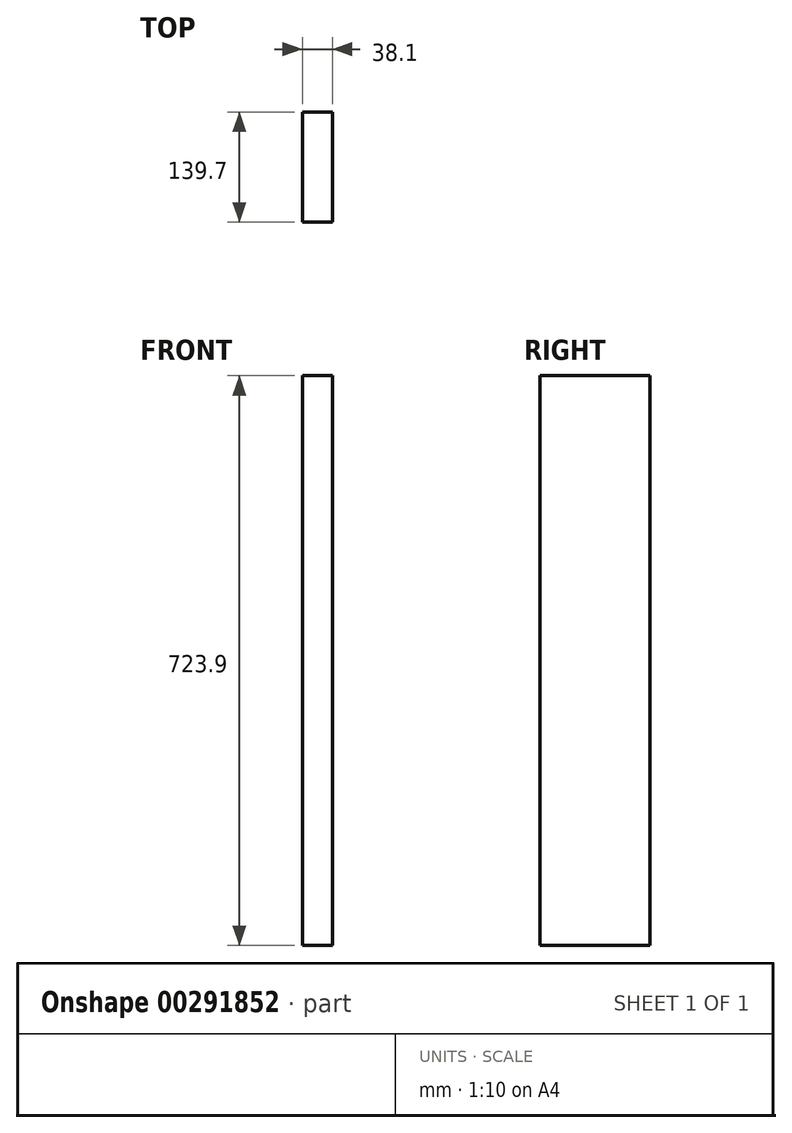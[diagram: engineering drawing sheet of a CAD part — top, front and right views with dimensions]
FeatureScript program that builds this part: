
annotation { "Feature Type Name" : "Feature", "Feature Type Description" : "" }
export const myFeature = defineFeature(function(context is Context, id is Id, definition is map)
    precondition{}
    {
        {
            var Q0;
            Q0=qCreatedBy(makeId("Top.planeOp"),FACE);
            var sketch = newSketch(context, id + "F0", { "sketchPlane" : qUnion([Q0])});
            skLineSegment(sketch, "E0.bottom", {"start": v(19.05, 69.85) * mm, "end": v(-19.05, 69.85) * mm});
            skLineSegment(sketch, "E0.top", {"start": v(19.05, -69.85) * mm, "end": v(-19.05, -69.85) * mm});
            skLineSegment(sketch, "E0.left", {"start": v(19.05, 69.85) * mm, "end": v(19.05, -69.85) * mm});
            skLineSegment(sketch, "E0.right", {"start": v(-19.05, 69.85) * mm, "end": v(-19.05, -69.85) * mm});
            skPoint(sketch, "E0.middle", {"position": v(0, 0) * mm});
            skSolve(sketch);
        }
        {
            var Q0;
            Q0 = qSketchRegion(id + "F0", true);
            extrude(context, id + "F1", {"entities" : qUnion([Q0]), "endBound" : BoundingType.SYMMETRIC, "depth" : 723.9 * mm});
        }
    });
